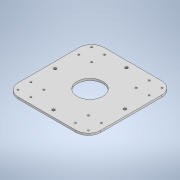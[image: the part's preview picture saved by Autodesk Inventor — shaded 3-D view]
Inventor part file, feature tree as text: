
AUTODESK INVENTOR PART (.ipt)
format: ipt  version: 2021 (Build 250183000, 183)  size: 184,832 bytes
history: native  units: mm
features: other x4, extrude x1, sketch x1, projected_geometry x1
ambient origin geometry x8: Origin, YZ Plane, XZ Plane, XY Plane, X Axis, Y Axis, Z Axis, Center Point
bodies: Body1 (feature_tree)
feature tree (7):
  other  "頸部殼件 - 拆件.ipt"
  extrude  "擠出1"  Depth=10.0mm
  other  "實體3::頸部殼件 - 拆件.ipt"
  other  "標籤特徵1"
  sketch  "草圖1"
  projected_geometry  "投影迴路1"
  other  "實體1"
